# Revit family: Magnuson-Drop-Waste_Bin-Without_Lid-1
name_source: partatom
category: Furniture
revit_build: Autodesk Revit 2014 (Build: 20130308_1515(x64)
units: mm (PartAtom-declared; Revit-internal decimal feet)

## types (3) — shared parameters
Assembly Code = E2020200
Keynote = 12500
Low Emitting Finish = Yes
Low Emitting Material = Yes
Manufacturer = Magnuson Group
Painted Steel = Forged Grey
Salvage or Reuse = Yes
Type Comments = Drop Waste Receptacles
URL = www.magnusongroup.com
zero-valued in all types: Cost, Percentage of Recycled Content

## per-type parameters (varying)
| type | Depth | Description | Height | Width |
| Drop-10 | 220.000 mm | Metal waste bin with stainless steel bag ring. Capacity 7.66 gallons | 373.000 mm | 350.000 mm |
| Drop-20 | 180.000 mm | Metal waste bin with stainless steel bag ring. Capacity 9.51 gallons | 480.000 mm | 420.000 mm |
| Drop Mini | 220.000 mm | Metal waste bin with stainless steel bag ring. Capacity 9.51 gallons | 300.000 mm | 220.000 mm |

note: column(s) folded — value = type name in every type: Model

## geometry (parser evidence)
native form markers: Sweep x3
no freeform markers — native parametric forms only
